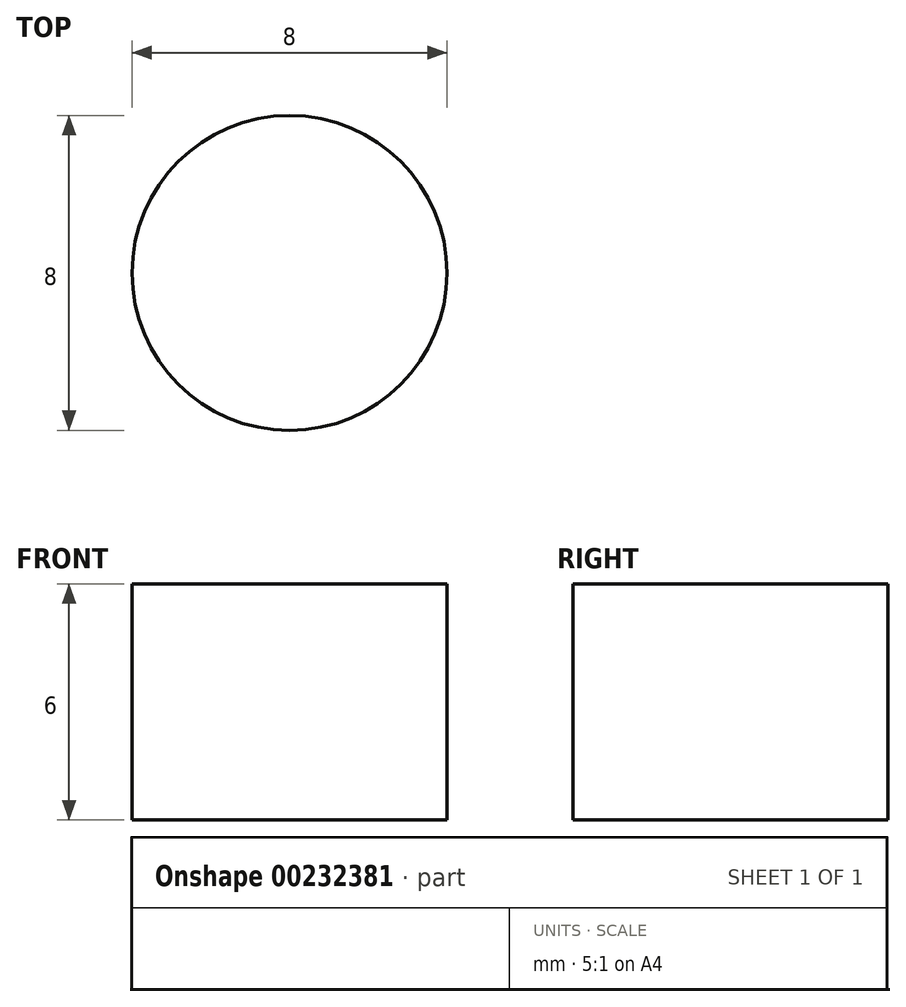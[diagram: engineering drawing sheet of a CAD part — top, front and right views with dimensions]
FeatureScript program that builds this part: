
annotation { "Feature Type Name" : "Feature", "Feature Type Description" : "" }
export const myFeature = defineFeature(function(context is Context, id is Id, definition is map)
    precondition{}
    {
        {
            var Q0;
            Q0=qCreatedBy(makeId("Top.planeOp"),FACE);
            var sketch = newSketch(context, id + "F0", { "sketchPlane" : qUnion([Q0])});
            skCircle(sketch, "E0", {"center": v(0, 0) * mm, "radius": 4 * mm});
            skSolve(sketch);
        }
        {
            var Q0;
            Q0=makeQuery(id+"F0.imprint","IMPRINT",FACE,{"disambiguationData":[TD([[makeQuery(id+"F0.imprint","IMPRINT",EDGE,{"derivedFrom":sQuery(id+"F0.wireOp",EDGE,"E0")}),1.0]])]});
            extrude(context, id + "F1", {"entities" : qUnion([Q0]), "flatOperationType" : FlatOperationType.REMOVE, "offsetDistance" : 25.4 * mm, "depth" : 3 * mm, "domain" : OperationDomain.MODEL});
        }
        {
            var Q0;
            Q0=makeQuery(id+"F1.opExtrude","SWEPT_BODY",BODY,{"disambiguationData":[OSD([sQuery(id+"F0.wireOp",EDGE,"E0")])]});
            var Q1;
            Q1=qCreatedBy(makeId("Top.planeOp"),FACE);
            mirror(context, id + "F2", {"operationType" : NewBodyOperationType.ADD, "entities" : qUnion([Q0]), "mirrorPlane" : qUnion([Q1])});
        }
    });
